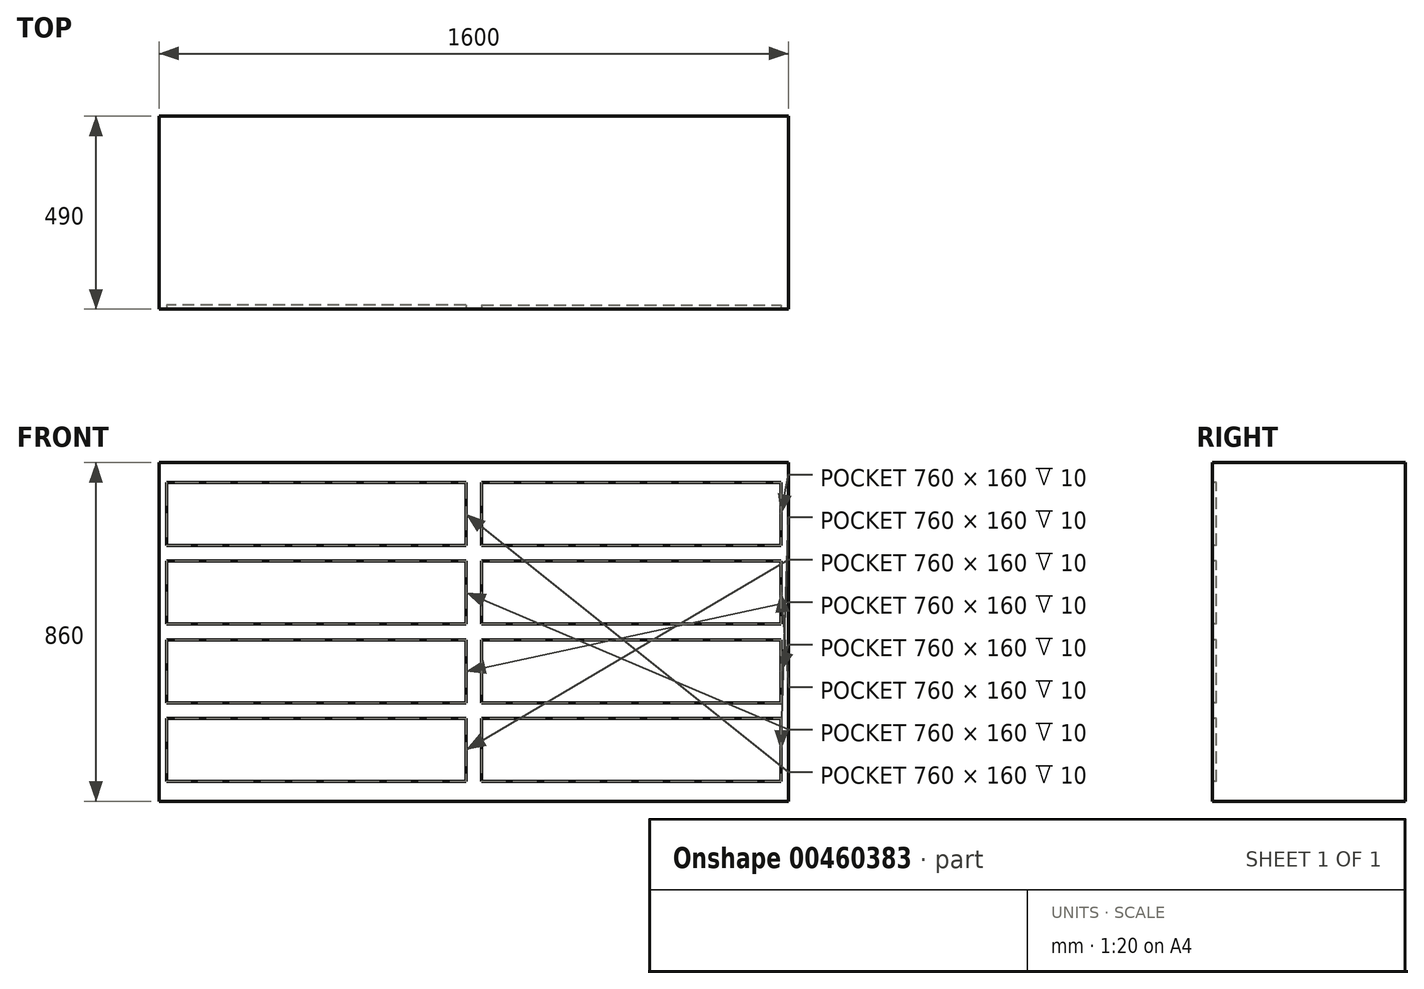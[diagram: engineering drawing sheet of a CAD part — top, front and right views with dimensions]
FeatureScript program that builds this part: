
annotation { "Feature Type Name" : "Feature", "Feature Type Description" : "" }
export const myFeature = defineFeature(function(context is Context, id is Id, definition is map)
    precondition{}
    {
        {
            var Q0;
            Q0=qCreatedBy(makeId("Top.planeOp"),FACE);
            var sketch = newSketch(context, id + "F0", { "sketchPlane" : qUnion([Q0])});
            skLineSegment(sketch, "E0.bottom", {"start": v(800, 245) * mm, "end": v(-800, 245) * mm});
            skLineSegment(sketch, "E0.top", {"start": v(800, -245) * mm, "end": v(-800, -245) * mm});
            skLineSegment(sketch, "E0.left", {"start": v(800, 245) * mm, "end": v(800, -245) * mm});
            skLineSegment(sketch, "E0.right", {"start": v(-800, 245) * mm, "end": v(-800, -245) * mm});
            skPoint(sketch, "E0.middle", {"position": v(0, 0) * mm});
            skSolve(sketch);
        }
        {
            var Q0;
            Q0 = qSketchRegion(id + "F0", true);
            extrude(context, id + "F1", {"entities" : qUnion([Q0]), "depth" : 860 * mm});
        }
        {
            var Q0;
            Q0=makeQuery(id+"F1.opExtrude","SWEPT_FACE",FACE,{"disambiguationData":[OSD([sQuery(id+"F0.wireOp",EDGE,"E0.top")])]});
            var sketch = newSketch(context, id + "F2", { "sketchPlane" : qUnion([Q0])});
            skLineSegment(sketch, "E1", {"start": v(0, 0) * mm, "end": v(0, 860) * mm, "construction": true});
            skLineSegment(sketch, "E2", {"start": v(0, 430) * mm, "end": v(800, 430) * mm, "construction": true});
            skLineSegment(sketch, "E3", {"start": v(0, 630) * mm, "end": v(800, 630) * mm, "construction": true});
            skLineSegment(sketch, "E4", {"start": v(0, 830) * mm, "end": v(800, 830) * mm, "construction": true});
            skLineSegment(sketch, "E5", {"start": v(0, 630) * mm, "end": v(-800, 630) * mm, "construction": true});
            skLineSegment(sketch, "E6", {"start": v(0, 830) * mm, "end": v(-800, 830) * mm, "construction": true});
            skLineSegment(sketch, "E7", {"start": v(0, 430) * mm, "end": v(-800, 430) * mm, "construction": true});
            skLineSegment(sketch, "E8", {"start": v(0, 230) * mm, "end": v(800, 230) * mm, "construction": true});
            skLineSegment(sketch, "E9", {"start": v(0, 30) * mm, "end": v(800, 30) * mm, "construction": true});
            skLineSegment(sketch, "E10.MirrorCS", {"start": v(0, 230) * mm, "end": v(-800, 230) * mm, "construction": true});
            skLineSegment(sketch, "E11.MirrorCS", {"start": v(0, 30) * mm, "end": v(-800, 30) * mm, "construction": true});
            skLineSegment(sketch, "E12.0", {"start": v(780, 810) * mm, "end": v(780, 650) * mm});
            skLineSegment(sketch, "E13.trimOffspring", {"start": v(20, 650) * mm, "end": v(20, 810) * mm});
            skLineSegment(sketch, "E14", {"start": v(20, 810) * mm, "end": v(780, 810) * mm});
            skLineSegment(sketch, "E15", {"start": v(780, 650) * mm, "end": v(20, 650) * mm});
            skLineSegment(sketch, "E16.0.1.0", {"start": v(20, 450) * mm, "end": v(20, 610) * mm});
            skLineSegment(sketch, "E16.0.1.1", {"start": v(20, 610) * mm, "end": v(780, 610) * mm});
            skLineSegment(sketch, "E16.0.1.2", {"start": v(780, 610) * mm, "end": v(780, 450) * mm});
            skLineSegment(sketch, "E16.0.1.3", {"start": v(780, 450) * mm, "end": v(20, 450) * mm});
            skLineSegment(sketch, "E16.0.2.0", {"start": v(20, 250) * mm, "end": v(20, 410) * mm});
            skLineSegment(sketch, "E16.0.2.1", {"start": v(20, 410) * mm, "end": v(780, 410) * mm});
            skLineSegment(sketch, "E16.0.2.2", {"start": v(780, 410) * mm, "end": v(780, 250) * mm});
            skLineSegment(sketch, "E16.0.2.3", {"start": v(780, 250) * mm, "end": v(20, 250) * mm});
            skLineSegment(sketch, "E16.0.3.0", {"start": v(20, 50) * mm, "end": v(20, 210) * mm});
            skLineSegment(sketch, "E16.0.3.1", {"start": v(20, 210) * mm, "end": v(780, 210) * mm});
            skLineSegment(sketch, "E16.0.3.2", {"start": v(780, 210) * mm, "end": v(780, 50) * mm});
            skLineSegment(sketch, "E16.0.3.3", {"start": v(780, 50) * mm, "end": v(20, 50) * mm});
            skLineSegment(sketch, "E16.1.0.0", {"start": v(-780, 650) * mm, "end": v(-780, 810) * mm});
            skLineSegment(sketch, "E16.1.0.1", {"start": v(-780, 810) * mm, "end": v(-20, 810) * mm});
            skLineSegment(sketch, "E16.1.0.2", {"start": v(-20, 810) * mm, "end": v(-20, 650) * mm});
            skLineSegment(sketch, "E16.1.0.3", {"start": v(-20, 650) * mm, "end": v(-780, 650) * mm});
            skLineSegment(sketch, "E16.1.1.0", {"start": v(-780, 450) * mm, "end": v(-780, 610) * mm});
            skLineSegment(sketch, "E16.1.1.1", {"start": v(-780, 610) * mm, "end": v(-20, 610) * mm});
            skLineSegment(sketch, "E16.1.1.2", {"start": v(-20, 610) * mm, "end": v(-20, 450) * mm});
            skLineSegment(sketch, "E16.1.1.3", {"start": v(-20, 450) * mm, "end": v(-780, 450) * mm});
            skLineSegment(sketch, "E16.1.2.0", {"start": v(-780, 250) * mm, "end": v(-780, 410) * mm});
            skLineSegment(sketch, "E16.1.2.1", {"start": v(-780, 410) * mm, "end": v(-20, 410) * mm});
            skLineSegment(sketch, "E16.1.2.2", {"start": v(-20, 410) * mm, "end": v(-20, 250) * mm});
            skLineSegment(sketch, "E16.1.2.3", {"start": v(-20, 250) * mm, "end": v(-780, 250) * mm});
            skLineSegment(sketch, "E16.1.3.0", {"start": v(-780, 50) * mm, "end": v(-780, 210) * mm});
            skLineSegment(sketch, "E16.1.3.1", {"start": v(-780, 210) * mm, "end": v(-20, 210) * mm});
            skLineSegment(sketch, "E16.1.3.2", {"start": v(-20, 210) * mm, "end": v(-20, 50) * mm});
            skLineSegment(sketch, "E16.1.3.3", {"start": v(-20, 50) * mm, "end": v(-780, 50) * mm});
            skLineSegment(sketch, "E16.direction1", {"start": v(20, 650) * mm, "end": v(-780, 650) * mm, "construction": true});
            skLineSegment(sketch, "E16.direction2", {"start": v(20, 650) * mm, "end": v(20, 450) * mm, "construction": true});
            skSolve(sketch);
        }
        {
            var Q0;
            Q0=makeQuery(id+"F2.imprint","IMPRINT",FACE,{"disambiguationData":[TD([[makeQuery(id+"F2.imprint","IMPRINT",EDGE,{"derivedFrom":sQuery(id+"F2.wireOp",EDGE,"E12.0")}),-1.0]])]});
            var Q1;
            Q1=makeQuery(id+"F2.imprint","IMPRINT",FACE,{"disambiguationData":[TD([[makeQuery(id+"F2.imprint","IMPRINT",EDGE,{"derivedFrom":sQuery(id+"F2.wireOp",EDGE,"E16.1.0.0")}),-1.0]])]});
            var Q2;
            Q2=makeQuery(id+"F2.imprint","IMPRINT",FACE,{"disambiguationData":[TD([[makeQuery(id+"F2.imprint","IMPRINT",EDGE,{"derivedFrom":sQuery(id+"F2.wireOp",EDGE,"E16.1.1.0")}),-1.0]])]});
            var Q3;
            Q3=makeQuery(id+"F2.imprint","IMPRINT",FACE,{"disambiguationData":[TD([[makeQuery(id+"F2.imprint","IMPRINT",EDGE,{"derivedFrom":sQuery(id+"F2.wireOp",EDGE,"E16.0.1.0")}),-1.0]])]});
            var Q4;
            Q4=makeQuery(id+"F2.imprint","IMPRINT",FACE,{"disambiguationData":[TD([[makeQuery(id+"F2.imprint","IMPRINT",EDGE,{"derivedFrom":sQuery(id+"F2.wireOp",EDGE,"E16.0.2.0")}),-1.0]])]});
            var Q5;
            Q5=makeQuery(id+"F2.imprint","IMPRINT",FACE,{"disambiguationData":[TD([[makeQuery(id+"F2.imprint","IMPRINT",EDGE,{"derivedFrom":sQuery(id+"F2.wireOp",EDGE,"E16.1.2.0")}),-1.0]])]});
            var Q6;
            Q6=makeQuery(id+"F2.imprint","IMPRINT",FACE,{"disambiguationData":[TD([[makeQuery(id+"F2.imprint","IMPRINT",EDGE,{"derivedFrom":sQuery(id+"F2.wireOp",EDGE,"E16.1.3.0")}),-1.0]])]});
            var Q7;
            Q7=makeQuery(id+"F2.imprint","IMPRINT",FACE,{"disambiguationData":[TD([[makeQuery(id+"F2.imprint","IMPRINT",EDGE,{"derivedFrom":sQuery(id+"F2.wireOp",EDGE,"E16.0.3.0")}),-1.0]])]});
            extrude(context, id + "F3", {"entities" : qUnion([Q0, Q1, Q2, Q3, Q4, Q5, Q6, Q7]), "operationType" : NewBodyOperationType.REMOVE, "oppositeDirection" : true, "depth" : 10 * mm});
        }
    });
